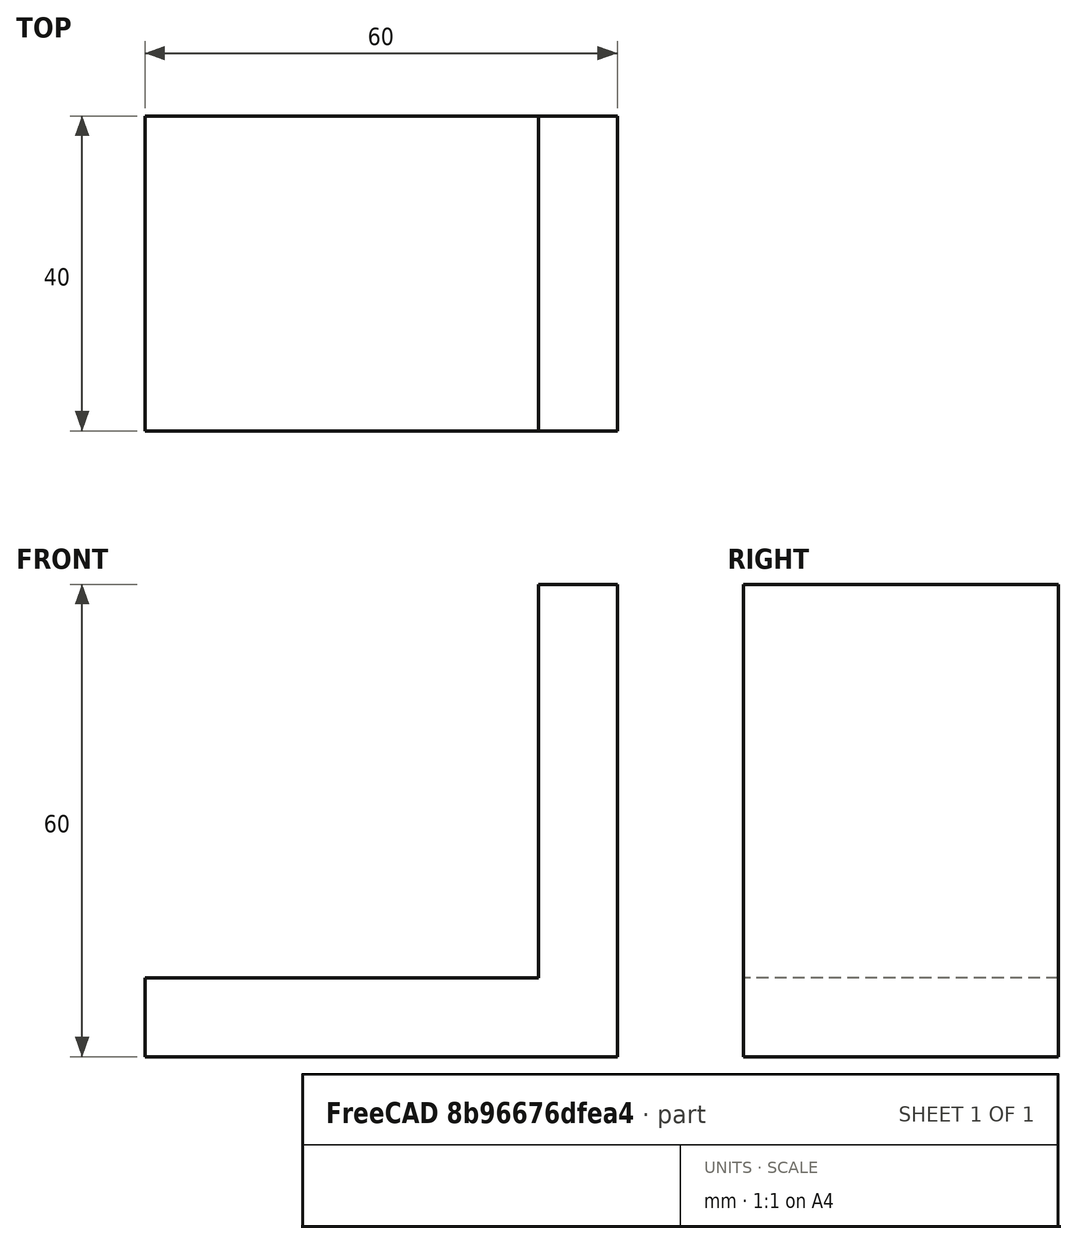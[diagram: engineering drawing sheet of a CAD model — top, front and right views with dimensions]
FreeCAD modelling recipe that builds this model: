
FCSTD DOCUMENT  (FreeCAD 0.21R33771 (Git))
Label: L_corner
License: All rights reserved
LicenseURL: http://en.wikipedia.org/wiki/All_rights_reserved
objects: Sketcher::SketchObject×1, PartDesign::Pad×1, PartDesign::Body×1, Spreadsheet::Sheet×1
note: 4 computed .brp shape members not serialized (recipe doc carries the construction recipe); baked Part::Feature solids carry a one-line shape summary decoded from their .brp

FEATURE [Sketcher::SketchObject] Sketch
  FullyConstrained = true
  MapMode = 5
  Placement = pos=(0,0,0) rot=(1,0,0;1.5708rad)
  Support = -> [XZ_Plane]
  expr: Constraints[15] = <<d>>.side
  sketch-geometry (6):
    g0: LineSegment StartX=-60 StartY=0 StartZ=0 EndX=0 EndY=0 EndZ=0
    g1: LineSegment StartX=0 StartY=0 StartZ=0 EndX=0 EndY=60 EndZ=0
    g2: LineSegment StartX=0 StartY=60 StartZ=0 EndX=-10 EndY=60 EndZ=0
    g3: LineSegment StartX=-10 StartY=60 StartZ=0 EndX=-10 EndY=10 EndZ=0
    g4: LineSegment StartX=-10 StartY=10 StartZ=0 EndX=-60 EndY=10 EndZ=0
    g5: LineSegment StartX=-60 StartY=10 StartZ=0 EndX=-60 EndY=0 EndZ=0
  constraints (17):
    c: PointOnObject(g0,g-1)
    c: Coincident(g0,g-1)
    c: Coincident(g0,g1)
    c: PointOnObject(g1,g-2)
    c: Coincident(g1,g2)
    c: Coincident(g2,g3)
    c: Vertical(g3)
    c: Coincident(g3,g4)
    c: Horizontal(g4)
    c: Coincident(g4,g5)
    c: Coincident(g5,g0)
    c: Vertical(g5)
    c: Horizontal(g2)
    c: Equal(g3,g4)
    c: Equal(g5,g2)
    c: DistanceX(g0,g0) = 60
    c: DistanceX(g2,g2) = 10
FEATURE [PartDesign::Pad] Pad
  Direction = (0,-1,-2e-16)
  Length = 40
  Length2 = 10
  Midplane = true
  Placement = pos=(0,0,0) rot=(1,0,0;1.5708rad)
  Profile = -> Sketch
  ReferenceAxis = -> Sketch [N_Axis]
  Type = 0
  expr: Length = <<d>>.width
FEATURE [PartDesign::Body] Body
  Group = -> [Sketch,Pad]
  Origin = -> Origin
  Tip = -> Pad
FEATURE [Spreadsheet::Sheet] Spreadsheet  label="d"
  cells = A1='side; B1(side)=60; A2='width; B2(width)=40; A3='holes_diam; B3(holes_diam)=10
